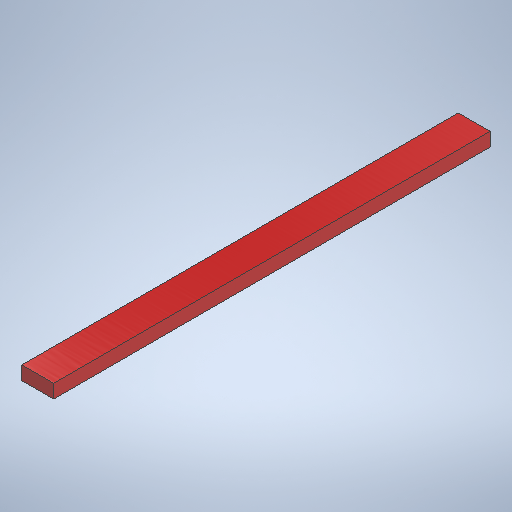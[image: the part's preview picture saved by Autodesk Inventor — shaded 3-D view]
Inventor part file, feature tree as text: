
AUTODESK INVENTOR PART (.ipt)
format: ipt  version: 2025.1 (Build 291241020, 241B)  size: 250,880 bytes
history: native  units: in
note: dims shown in document units (in); Inventor stores cm internally (conversion verified against a paired STEP export)
features: extrude x1, sketch x1, other x1
ambient origin geometry x8: Origin, YZ Plane, XZ Plane, XY Plane, X Axis, Y Axis, Z Axis, Center Point
bodies: Solid1 (feature_tree)
feature tree (3):
  extrude  "Extrusion1"  Depth=3.5in
  sketch  "Sketch1"  dims[d0=1.5in d1=3.5in d2=48.0in d3=0.0in]
  other  "Finish1"
